# Revit family: Считыватель AGRG SH-C_на гарни
name_source: partatom
category: Охранная сигнализация
units: mm (PartAtom-declared; Revit-internal decimal feet)

## family parameters
Общий = Нет
Основа = Грань
При загрузке вырезать с полостями = Нет
Размер круглого соединителя = Использовать диаметр
Сохранять ориентацию аннотаций = Нет
Тип детали = Нормальный
Точка расчета площади = Нет

## types (1)
- Считыватель AGRG SH-C_на гарни
    ADSK_Верхний порог напряжения = 15 В
    ADSK_Группирование = 1. Оборудование
    ADSK_Единица измерения = шт.
    ADSK_Завод-изготовитель = ООО «Агрегатор»
    ADSK_Код изделия = ESCTLSHC
    ADSK_Количество = 1
    ADSK_Марка = AGRG ЦОД
    ADSK_Масса = 0.7
    ADSK_Наименование = Ручка AGRG SH-С с электронным замком, встроенным мультиформатным считывателем карт и кодовой панелью для защиты и контроля доступа к телекоммуникационным и другим шкафам. Поддерживаемый тип карт: MIFARE (UID);Mifare Mini, Mifare Classic, Mifare Plus SL1/SL3,Mifare DESFire (UID и чтение из защищеннойьобласти карты); Mifare ID (UID и чтение из защищенных секторов карты).Только карты пользователей (не карты программирования и инициализации);I-CODE (ISO15693) (UID);EM-Marine (UID);HID 125 кГц (UID);Indala (Motorola) (UID);NFC (при установке приложения на смартфон,только ОС Android). Интерфейсы: W-26,34,37,40,42,58, TM (DS1990A);в секторном режиме до W-64. Цвет черный. Работает с различными системами контроля и управления доступом.
    ADSK_Наименование краткое = Ручка с электронным замком, считывателем карт и кодонаборной панелью
    ADSK_Нижний порог напряжения = 9 В
    ADSK_Обозначение = RC
    ITV_SUB_УГО на структурной схеме = УГО_Считыватель с клавиатурой и защелкой
    URL = https://skud.agrg.ru
    Изображение типоразмера = RC_key_castle.png
    Материал = Пластмасса, непрозрачная, черная
    Описание = ITV
    Отметка по умолчанию = 1219 мм
